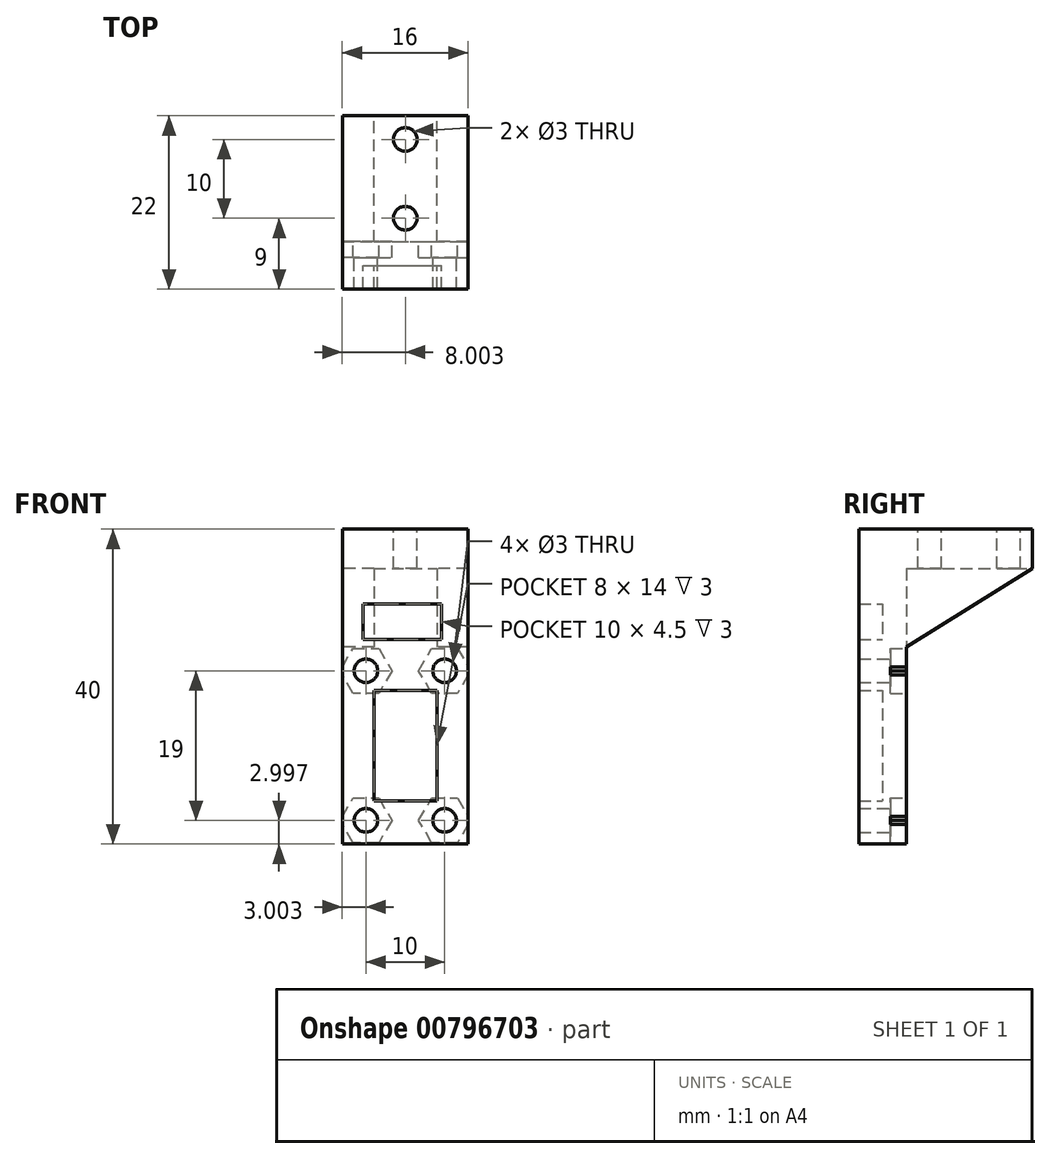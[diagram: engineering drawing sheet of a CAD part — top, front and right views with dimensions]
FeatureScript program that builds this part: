
annotation { "Feature Type Name" : "Feature", "Feature Type Description" : "" }
export const myFeature = defineFeature(function(context is Context, id is Id, definition is map)
    precondition{}
    {
        {
            var Q0;
            Q0=qCreatedBy(makeId("Front.planeOp"),FACE);
            var sketch = newSketch(context, id + "F0", { "sketchPlane" : qUnion([Q0])});
            skLineSegment(sketch, "E0.bottom", {"start": v(-7.36, 18.98) * mm, "end": v(8.64, 18.98) * mm});
            skLineSegment(sketch, "E0.top", {"start": v(-7.36, -21.02) * mm, "end": v(8.64, -21.02) * mm});
            skLineSegment(sketch, "E0.left", {"start": v(-7.36, 18.98) * mm, "end": v(-7.36, -21.02) * mm});
            skLineSegment(sketch, "E0.right", {"start": v(8.64, 18.98) * mm, "end": v(8.64, -21.02) * mm});
            skLineSegment(sketch, "E1.bottom", {"start": v(-3.36, -1.52) * mm, "end": v(4.64, -1.52) * mm});
            skLineSegment(sketch, "E1.top", {"start": v(-3.36, -15.52) * mm, "end": v(4.64, -15.52) * mm});
            skLineSegment(sketch, "E1.left", {"start": v(-3.36, -1.52) * mm, "end": v(-3.36, -15.52) * mm});
            skLineSegment(sketch, "E1.right", {"start": v(4.64, -1.52) * mm, "end": v(4.64, -15.52) * mm});
            skCircle(sketch, "E2", {"center": v(5.64, -18.02) * mm, "radius": 1.5 * mm});
            skCircle(sketch, "E3", {"center": v(5.64, 0.98) * mm, "radius": 1.5 * mm});
            skCircle(sketch, "E4", {"center": v(-4.36, 0.98) * mm, "radius": 1.5 * mm});
            skCircle(sketch, "E5", {"center": v(-4.36, -18.02) * mm, "radius": 1.5 * mm});
            skLineSegment(sketch, "E6.bottom", {"start": v(-4.75, 9.48) * mm, "end": v(5.25, 9.48) * mm});
            skLineSegment(sketch, "E6.top", {"start": v(-4.75, 4.98) * mm, "end": v(5.25, 4.98) * mm});
            skLineSegment(sketch, "E6.left", {"start": v(-4.75, 9.48) * mm, "end": v(-4.75, 4.98) * mm});
            skLineSegment(sketch, "E6.right", {"start": v(5.25, 9.48) * mm, "end": v(5.25, 4.98) * mm});
            skSolve(sketch);
        }
        {
            var Q0;
            Q0 = qSketchRegion(id + "F0", true);
            extrude(context, id + "F1", {"entities" : qUnion([Q0]), "depth" : 6 * mm, "offsetDistance" : 25 * mm});
        }
        {
            var Q0;
            Q0=makeQuery(id+"F0.imprint","IMPRINT",FACE,{"disambiguationData":[TD([[makeQuery(id+"F0.imprint","IMPRINT",EDGE,{"derivedFrom":sQuery(id+"F0.wireOp",EDGE,"E6.bottom")}),-1.0]])]});
            var Q1;
            Q1=makeQuery(id+"F0.imprint","IMPRINT",FACE,{"disambiguationData":[TD([[makeQuery(id+"F0.imprint","IMPRINT",EDGE,{"derivedFrom":sQuery(id+"F0.wireOp",EDGE,"E1.bottom")}),-1.0]])]});
            extrude(context, id + "F2", {"entities" : qUnion([Q0, Q1]), "operationType" : NewBodyOperationType.ADD, "depth" : 3 * mm, "offsetDistance" : 25 * mm});
        }
        {
            var Q0;
            Q0=makeQuery(id+"F1.opExtrude","SWEPT_FACE",FACE,{"disambiguationData":[OSD([sQuery(id+"F0.wireOp",EDGE,"E0.bottom")])]});
            var sketch = newSketch(context, id + "F3", { "sketchPlane" : qUnion([Q0])});
            skLineSegment(sketch, "E7.bottom", {"start": v(8.64, 0) * mm, "end": v(-7.36, 0) * mm});
            skLineSegment(sketch, "E7.top", {"start": v(8.64, 16) * mm, "end": v(-7.36, 16) * mm});
            skLineSegment(sketch, "E7.left", {"start": v(8.64, 0) * mm, "end": v(8.64, 16) * mm});
            skLineSegment(sketch, "E7.right", {"start": v(-7.36, 0) * mm, "end": v(-7.36, 16) * mm});
            skCircle(sketch, "E8", {"center": v(0.64, 13) * mm, "radius": 1.5 * mm});
            skCircle(sketch, "E9", {"center": v(0.64, 3) * mm, "radius": 1.5 * mm});
            skSolve(sketch);
        }
        {
            var Q0;
            Q0 = qSketchRegion(id + "F3", true);
            extrude(context, id + "F4", {"entities" : qUnion([Q0]), "operationType" : NewBodyOperationType.ADD, "oppositeDirection" : true, "depth" : 5 * mm, "offsetDistance" : 25 * mm});
        }
        {
            var Q0;
            Q0=makeQuery(id+"F4.opExtrude","CAP_FACE",FACE,{"disambiguationData":[OSD([sQuery(id+"F3.wireOp",EDGE,"E7.bottom"),sQuery(id+"F3.wireOp",EDGE,"E7.top"),sQuery(id+"F3.wireOp",EDGE,"E7.left"),sQuery(id+"F3.wireOp",EDGE,"E7.right"),sQuery(id+"F3.wireOp",EDGE,"E8"),sQuery(id+"F3.wireOp",EDGE,"E9")])],"isStart":false});
            var sketch = newSketch(context, id + "F5", { "sketchPlane" : qUnion([Q0])});
            skCircle(sketch, "E10.cCircle", {"center": v(0.64, -13) * mm, "radius": 2.85 * mm, "construction": true});
            skLineSegment(sketch, "E10.0", {"start": v(2.29, -15.85) * mm, "end": v(-1, -15.85) * mm});
            skLineSegment(sketch, "E10.1", {"start": v(-1, -15.85) * mm, "end": v(-2.65, -13) * mm});
            skLineSegment(sketch, "E10.2", {"start": v(-2.65, -13) * mm, "end": v(-1, -10.15) * mm});
            skLineSegment(sketch, "E10.3", {"start": v(-1, -10.15) * mm, "end": v(2.29, -10.15) * mm});
            skLineSegment(sketch, "E10.4", {"start": v(2.29, -10.15) * mm, "end": v(3.93, -13) * mm});
            skLineSegment(sketch, "E10.5", {"start": v(3.93, -13) * mm, "end": v(2.29, -15.85) * mm});
            skPoint(sketch, "E10.0.midPoint", {"position": v(0.64, -15.85) * mm});
            skCircle(sketch, "E11.cCircle", {"center": v(0.64, -3) * mm, "radius": 2.85 * mm, "construction": true});
            skLineSegment(sketch, "E11.0", {"start": v(2.29, -5.85) * mm, "end": v(-1, -5.85) * mm});
            skLineSegment(sketch, "E11.1", {"start": v(-1, -5.85) * mm, "end": v(-2.65, -3) * mm});
            skLineSegment(sketch, "E11.2", {"start": v(-2.65, -3) * mm, "end": v(-1, -0.15) * mm});
            skLineSegment(sketch, "E11.3", {"start": v(-1, -0.15) * mm, "end": v(2.29, -0.15) * mm});
            skLineSegment(sketch, "E11.4", {"start": v(2.29, -0.15) * mm, "end": v(3.93, -3) * mm});
            skLineSegment(sketch, "E11.5", {"start": v(3.93, -3) * mm, "end": v(2.29, -5.85) * mm});
            skPoint(sketch, "E11.0.midPoint", {"position": v(0.64, -5.85) * mm});
            skSolve(sketch);
        }
        {
            var Q0;
            Q0=makeQuery(id+"F0.imprint","IMPRINT",FACE,{"disambiguationData":[TD([[makeQuery(id+"F0.imprint","IMPRINT",EDGE,{"derivedFrom":sQuery(id+"F0.wireOp",EDGE,"E0.bottom")}),-1.0]])]});
            var sketch = newSketch(context, id + "F6", { "sketchPlane" : qUnion([Q0])});
            skCircle(sketch, "E12.cCircle", {"center": v(5.64, 0.98) * mm, "radius": 2.85 * mm, "construction": true});
            skLineSegment(sketch, "E12.0", {"start": v(4, 3.83) * mm, "end": v(7.29, 3.83) * mm});
            skLineSegment(sketch, "E12.1", {"start": v(7.29, 3.83) * mm, "end": v(8.93, 0.98) * mm});
            skLineSegment(sketch, "E12.2", {"start": v(8.93, 0.98) * mm, "end": v(7.29, -1.87) * mm});
            skLineSegment(sketch, "E12.3", {"start": v(7.29, -1.87) * mm, "end": v(4, -1.87) * mm});
            skLineSegment(sketch, "E12.4", {"start": v(4, -1.87) * mm, "end": v(2.35, 0.98) * mm});
            skLineSegment(sketch, "E12.5", {"start": v(2.35, 0.98) * mm, "end": v(4, 3.83) * mm});
            skPoint(sketch, "E12.0.midPoint", {"position": v(5.64, 3.83) * mm});
            skCircle(sketch, "E13.cCircle", {"center": v(-4.36, 0.98) * mm, "radius": 2.85 * mm, "construction": true});
            skLineSegment(sketch, "E13.0", {"start": v(-6, 3.83) * mm, "end": v(-2.71, 3.83) * mm});
            skLineSegment(sketch, "E13.1", {"start": v(-2.71, 3.83) * mm, "end": v(-1.07, 0.98) * mm});
            skLineSegment(sketch, "E13.2", {"start": v(-1.07, 0.98) * mm, "end": v(-2.71, -1.87) * mm});
            skLineSegment(sketch, "E13.3", {"start": v(-2.71, -1.87) * mm, "end": v(-6, -1.87) * mm});
            skLineSegment(sketch, "E13.4", {"start": v(-6, -1.87) * mm, "end": v(-7.65, 0.98) * mm});
            skLineSegment(sketch, "E13.5", {"start": v(-7.65, 0.98) * mm, "end": v(-6, 3.83) * mm});
            skPoint(sketch, "E13.0.midPoint", {"position": v(-4.36, 3.83) * mm});
            skCircle(sketch, "E14.cCircle", {"center": v(-4.36, -18.02) * mm, "radius": 2.85 * mm, "construction": true});
            skLineSegment(sketch, "E14.0", {"start": v(-6, -15.17) * mm, "end": v(-2.71, -15.17) * mm});
            skLineSegment(sketch, "E14.1", {"start": v(-2.71, -15.17) * mm, "end": v(-1.07, -18.02) * mm});
            skLineSegment(sketch, "E14.2", {"start": v(-1.07, -18.02) * mm, "end": v(-2.71, -20.87) * mm});
            skLineSegment(sketch, "E14.3", {"start": v(-2.71, -20.87) * mm, "end": v(-6, -20.87) * mm});
            skLineSegment(sketch, "E14.4", {"start": v(-6, -20.87) * mm, "end": v(-7.65, -18.02) * mm});
            skLineSegment(sketch, "E14.5", {"start": v(-7.65, -18.02) * mm, "end": v(-6, -15.17) * mm});
            skPoint(sketch, "E14.0.midPoint", {"position": v(-4.36, -15.17) * mm});
            skCircle(sketch, "E15.cCircle", {"center": v(5.64, -18.02) * mm, "radius": 2.85 * mm, "construction": true});
            skLineSegment(sketch, "E15.0", {"start": v(4, -15.17) * mm, "end": v(7.29, -15.17) * mm});
            skLineSegment(sketch, "E15.1", {"start": v(7.29, -15.17) * mm, "end": v(8.93, -18.02) * mm});
            skLineSegment(sketch, "E15.2", {"start": v(8.93, -18.02) * mm, "end": v(7.29, -20.87) * mm});
            skLineSegment(sketch, "E15.3", {"start": v(7.29, -20.87) * mm, "end": v(4, -20.87) * mm});
            skLineSegment(sketch, "E15.4", {"start": v(4, -20.87) * mm, "end": v(2.35, -18.02) * mm});
            skLineSegment(sketch, "E15.5", {"start": v(2.35, -18.02) * mm, "end": v(4, -15.17) * mm});
            skPoint(sketch, "E15.0.midPoint", {"position": v(5.64, -15.17) * mm});
            skSolve(sketch);
        }
        {
            var Q0;
            Q0 = qSketchRegion(id + "F6", true);
            extrude(context, id + "F7", {"entities" : qUnion([Q0]), "operationType" : NewBodyOperationType.REMOVE, "depth" : 2 * mm, "offsetDistance" : 25 * mm});
        }
        {
            var Q0;
            Q0=makeQuery(id+"F4.boolean.opBoolean","MERGE",FACE,{"derivedFrom":[makeQuery(id+"F1.opExtrude","SWEPT_FACE",FACE,{"disambiguationData":[OSD([sQuery(id+"F0.wireOp",EDGE,"E0.left")])]}),makeQuery(id+"F4.opExtrude","SWEPT_FACE",FACE,{"disambiguationData":[OSD([sQuery(id+"F3.wireOp",EDGE,"E7.right")])]})]});
            var sketch = newSketch(context, id + "F8", { "sketchPlane" : qUnion([Q0])});
            skLineSegment(sketch, "E16", {"start": v(0, 3.98) * mm, "end": v(-16, 13.98) * mm});
            skLineSegment(sketch, "E17", {"start": v(-16, 13.98) * mm, "end": v(0, 13.98) * mm});
            skLineSegment(sketch, "E18", {"start": v(0, 13.98) * mm, "end": v(0, 3.98) * mm});
            skSolve(sketch);
        }
        {
            var Q0;
            Q0 = qSketchRegion(id + "F8", true);
            extrude(context, id + "F9", {"entities" : qUnion([Q0]), "operationType" : NewBodyOperationType.ADD, "oppositeDirection" : true, "depth" : 4 * mm, "offsetDistance" : 25 * mm});
        }
        {
            var Q0;
            Q0=makeQuery(id+"F8.imprint","IMPRINT",FACE,{"disambiguationData":[TD([[makeQuery(id+"F8.imprint","IMPRINT",EDGE,{"derivedFrom":sQuery(id+"F8.wireOp",EDGE,"E16")}),-1.0]])]});
            extrude(context, id + "F10", {"entities" : qUnion([Q0]), "operationType" : NewBodyOperationType.ADD, "oppositeDirection" : true, "depth" : 16 * mm, "offsetDistance" : 25 * mm, "hasSecondDirection" : true, "secondDirectionOppositeDirection" : true, "secondDirectionDepth" : 12 * mm});
        }
    });
